# Revit family: 7826
name_source: partatom
category: Lighting Fixtures
revit_build: Autodesk Revit 2018 (Build: 20170223_1515(x64)
units: mm (PartAtom-declared; Revit-internal decimal feet)

## family parameters
Cut with Voids When Loaded = No
Host = Face
Light Source = Yes
OmniClass Number = 23.80.70.00
OmniClass Title = Lighting
Part Type = Normal
Room Calculation Point = No
Round Connector Dimension = Use Diameter
Shared = No

## types (1)
- 0007826 PIXO LINE 1500 UGR19 840 BLACK
    Apparent Load = 50 VA
    Assembly Code = D5020200
    AssetType = Fixed
    ClassificationName = Uniclass2015
    ClassificationValue = EF_70_80
    Color Filter = 16777215
    Cost = 0 $
    Default Elevation = 1219 mm
    Description = Pixo Line is a linear track system, adds flexibility to any space due the variety of product options
Offers an easy installation with two separate modules
Push-in/push-out mechanism with GR6d-15 connector
Compatible with Zhaga Book 14
Aluminium body, plastic end caps,aluminised plastic low glare optics in a single line configuration, light beam angle:70°
Textured black finishing colour.
Light color temperature: 4000K, neutral white, max. system power: 50W
Max. fixture lumen output: 7500lm, efficacy: 150lm/W, Ra80 typical, LED chromacity: 3 step MacAdam ellipse (SDCM3), IR/UV free light source without heat radiation
Multipower driver module with 8 power settings meet all installation needs with one single product (selection between 17W, 19W, 24W, 29W, 34W, 38W, 43W, 50W)
Suitable for installation on 3-circuit tracks, please check compatibility list on the instruction sheet. Compatible with OneTrack
Electrical protection: Class III. Degree of protection: IP20, suitable for indoor environment only
Light modules should be combined with suitable in-track drivers
Nominal product dimensions: L.1464mmx37.4mmx37mm
    Dimming Lamp Color Temperature Shift = <None>
    DocumentationLiterature = http://www.sylvania-lighting.com
    ElectricShockClassification = 150
    Emit Shape Visible in Rendering = No
    Emit from Circle Diameter = 610 mm
    IfcExportAs = Class III
    IfcExportType = IfcLightFixtureType
    ImpactProtectionIndex = IfcLightFixtureType
    IngressProtection = IfcLightFixtureType
    InputNominalFrequency = 4000
    InputVoltage = 0
    LampColourRenderingIndex = 16500
    LampColourTemperature = LED
    LampMacAdamStep = 80
    LampNominalLuminous = 4000 K
    LightOutputRatio = LED
    LuminaireType = 0
    ManufacturerName = 150 lm/W
    Material = Feilo Sylvania
    Material_1_SYL = <By Category>
    Material_2_SYL = <By Category>
    Material_3_SYL = <By Category>
    Material_4_SYL = <By Category>
    Model = PIXO LINE 1500 UGR19 840 BLACK
    ModelNumber = 0007826
    ModelReference = PIXO LINE 1500 UGR19 840 BLACK
    Name = PIXO LINE 1500 UGR19 840 BLACK
    NominalDepth = 37 mm  [stored 0.121391 ft]
    NominalHeight = 38 mm
    NominalLength = 37 mm  [stored 0.121391 ft]
    Photometric Web File = 0007826 -500mA.IES
    PowerConsumption = Lighting
    PowerFactor = 0
    Tilt Angle = -90.00°
    Type Image = <None>
    TypeName = PIXO LINE 1500 UGR19 840 BLACK
    URL = 0
    Voltage = 0 V
    WarrantyDescription = http://www.sylvania-lighting.com

note: [stored X ft] marks values corroborated as IEEE doubles in the binary element streams (Revit-internal decimal feet)

## geometry (parser evidence)
native form markers: Sweep x4
no freeform markers — native parametric forms only
